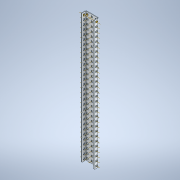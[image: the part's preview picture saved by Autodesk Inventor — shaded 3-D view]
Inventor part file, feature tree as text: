
AUTODESK INVENTOR PART (.ipt)
format: ipt  version: 2020 (Build 240168000, 168)  size: 1,400,320 bytes
history: native  units: in
note: dims shown in document units (in); Inventor stores cm internally (conversion verified against a paired STEP export)
features: other x153, plane x5, pattern_linear x3, split x1, sheet_metal_op x1
ambient origin geometry x8: Origin, YZ Plane, XZ Plane, XY Plane, X Axis, Y Axis, Z Axis, Center Point
bodies: Solid1 (feature_tree)
feature tree (163):
  plane  "Work Plane2"
  plane  "Work Plane1"
  other  "Work Point1"
  other  "Work Point2"
  other  "Work Axis1"
  other  "Work Axis2"
  other  "Work Axis3"
  pattern_linear  "Rectangular Pattern1"  Count1=30 Spacing1=0.5in
  pattern_linear  "Rectangular Pattern2"  Count1=30 Spacing1=0.5in
  pattern_linear  "Rectangular Pattern3"  Count1=30 Spacing1=0.5in
  plane  "Work Plane5"
  split  "Split1"
  plane  "Work Plane3"
  plane  "Work Plane4"
  other  "Work Point3"
  other  "Work Axis4"
  other  "Work Axis5"
  other  "Work Axis6"
  other  "Work Axis7"
  other  "Work Axis8"
  other  "Work Axis9"
  other  "Work Axis10"
  other  "Work Axis11"
  other  "Work Axis12"
  other  "Work Axis13"
  other  "Work Axis14"
  other  "Work Axis15"
  other  "Work Axis16"
  other  "Work Axis17"
  other  "Work Axis18"
  other  "Work Axis19"
  other  "Work Axis20"
  other  "Work Axis21"
  other  "Work Axis22"
  other  "Work Axis23"
  other  "Work Axis24"
  other  "Work Axis25"
  other  "Work Axis26"
  other  "Work Axis27"
  other  "Work Axis28"
  other  "Work Axis29"
  other  "Work Axis30"
  other  "Work Axis31"
  other  "Work Axis32"
  other  "Work Axis38"
  other  "Work Axis39"
  other  "Work Axis40"
  other  "Work Axis41"
  other  "Work Axis42"
  other  "Work Axis43"
  other  "Work Axis44"
  other  "Work Axis45"
  other  "Work Axis46"
  other  "Work Axis47"
  other  "Work Axis48"
  other  "Work Axis49"
  other  "Work Axis50"
  other  "Work Axis51"
  other  "Work Axis52"
  other  "Work Axis53"
  other  "Work Axis54"
  other  "Work Axis55"
  other  "Work Axis56"
  other  "Work Axis57"
  other  "Work Axis58"
  other  "Work Axis59"
  other  "Work Axis60"
  other  "Work Axis61"
  other  "Work Axis62"
  other  "Work Axis63"
  other  "Work Axis64"
  other  "Work Axis65"
  other  "Work Axis66"
  other  "Work Axis72"
  other  "Work Axis73"
  other  "Work Axis74"
  other  "Work Axis75"
  other  "Work Axis76"
  other  "Work Axis77"
  other  "Work Axis78"
  other  "Work Axis79"
  other  "Work Axis80"
  other  "Work Axis81"
  other  "Work Axis82"
  other  "Work Axis83"
  other  "Work Axis84"
  other  "Work Axis85"
  other  "Work Axis86"
  other  "Work Axis87"
  other  "Work Axis88"
  other  "Work Axis89"
  other  "Work Axis90"
  other  "Work Axis91"
  other  "Work Axis92"
  other  "Work Axis93"
  other  "Work Axis94"
  other  "Work Axis95"
  other  "Work Axis96"
  other  "Work Axis97"
  other  "Work Axis98"
  other  "Work Axis99"
  other  "Work Axis100"
  other  "Work Axis106"
  other  "Work Axis107"
  other  "Work Axis108"
  other  "Work Axis109"
  other  "Work Axis110"
  other  "Work Axis111"
  other  "Work Axis112"
  other  "Work Axis113"
  other  "Work Axis114"
  other  "Work Axis115"
  other  "Work Axis116"
  other  "Work Axis117"
  other  "Work Axis118"
  other  "Work Axis119"
  other  "Work Axis120"
  other  "Work Axis121"
  other  "Work Axis122"
  other  "Work Axis123"
  other  "Work Axis124"
  other  "Work Axis125"
  other  "Work Axis126"
  other  "Work Axis127"
  other  "Work Axis128"
  other  "Work Axis129"
  other  "Work Axis130"
  other  "Work Axis131"
  other  "Work Axis132"
  other  "Work Axis133"
  other  "Work Axis134"
  other  "Work Axis135"
  other  "Work Axis141"
  other  "Work Axis142"
  other  "Work Axis143"
  other  "Work Axis144"
  other  "Work Axis145"
  other  "Work Axis146"
  other  "Work Axis147"
  other  "Work Axis148"
  other  "Work Axis149"
  other  "Work Axis150"
  other  "Work Axis151"
  other  "Work Axis152"
  other  "Work Axis153"
  other  "Work Axis154"
  other  "Work Axis155"
  other  "Work Axis156"
  other  "Work Axis157"
  other  "Work Axis158"
  other  "Work Axis159"
  other  "Work Axis160"
  other  "Work Axis161"
  other  "Work Axis162"
  other  "Work Axis163"
  other  "Work Axis164"
  other  "Work Axis165"
  other  "Work Axis166"
  other  "Work Axis167"
  other  "Work Axis168"
  other  "Work Axis169"
  other  "Work Axis170"
  sheet_metal_op  "Fold1"
